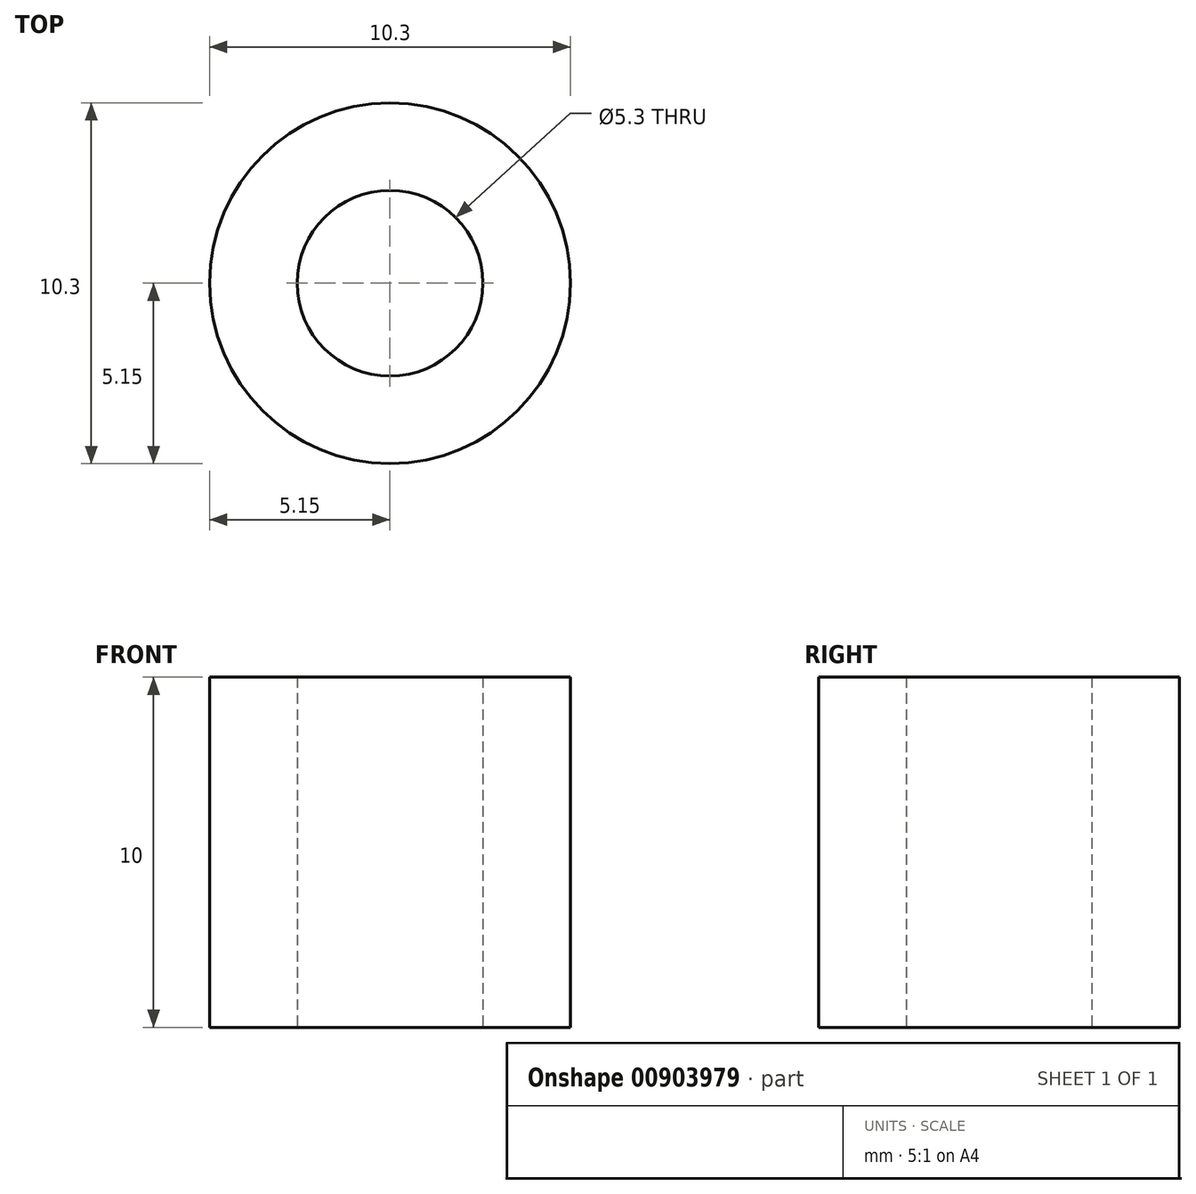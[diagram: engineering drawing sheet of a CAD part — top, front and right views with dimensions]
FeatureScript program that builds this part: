
annotation { "Feature Type Name" : "Feature", "Feature Type Description" : "" }
export const myFeature = defineFeature(function(context is Context, id is Id, definition is map)
    precondition{}
    {
        {
            var Q0;
            Q0=qCreatedBy(makeId("Top.planeOp"),FACE);
            var sketch = newSketch(context, id + "F0", { "sketchPlane" : qUnion([Q0])});
            skCircle(sketch, "E0", {"center": v(0, 0) * mm, "radius": 5.15 * mm});
            skCircle(sketch, "E1", {"center": v(0, 0) * mm, "radius": 2.65 * mm});
            skSolve(sketch);
        }
        {
            var Q0;
            Q0=qSketchRegion(id+"F0",true);
            extrude(context, id + "F1", {"entities" : qUnion([Q0]), "depth" : 10 * mm, "offsetDistance" : 25 * mm});
        }
    });
